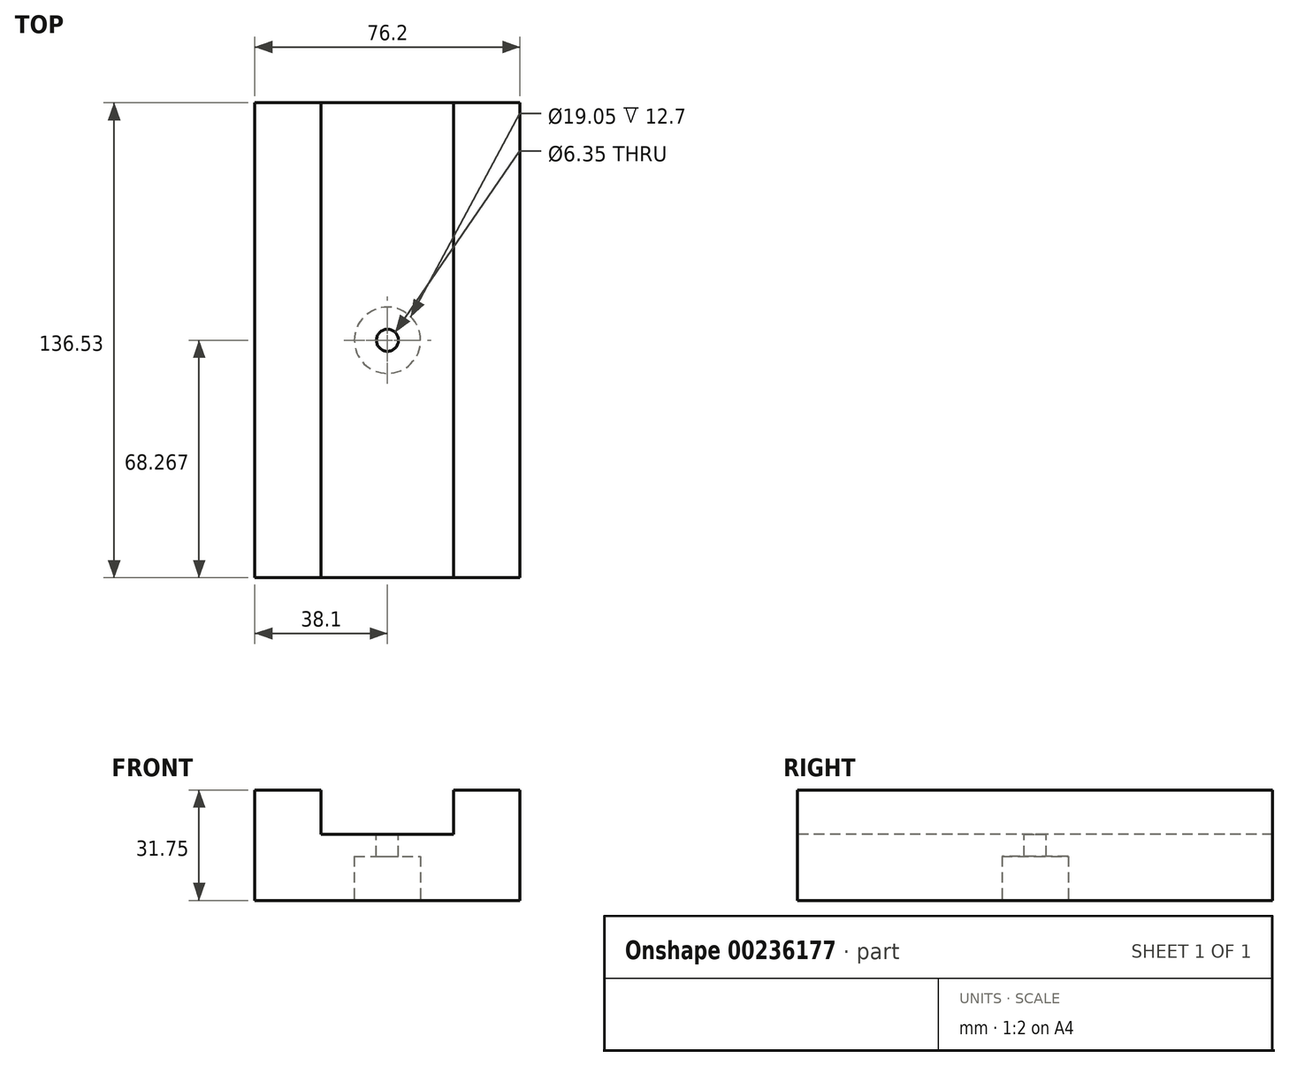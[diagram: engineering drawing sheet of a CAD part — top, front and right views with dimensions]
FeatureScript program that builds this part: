
annotation { "Feature Type Name" : "Feature", "Feature Type Description" : "" }
export const myFeature = defineFeature(function(context is Context, id is Id, definition is map)
    precondition{}
    {
        {
            var Q0;
            Q0=qCreatedBy(makeId("Front.planeOp"),FACE);
            var sketch = newSketch(context, id + "F0", { "sketchPlane" : qUnion([Q0])});
            skLineSegment(sketch, "E0", {"start": v(0, 0) * mm, "end": v(0, -31.75) * mm});
            skLineSegment(sketch, "E1", {"start": v(0, -31.75) * mm, "end": v(76.2, -31.75) * mm});
            skLineSegment(sketch, "E2", {"start": v(76.2, -31.75) * mm, "end": v(76.2, 0) * mm});
            skLineSegment(sketch, "E3", {"start": v(76.2, 0) * mm, "end": v(0, 0) * mm});
            skSolve(sketch);
        }
        {
            var Q0;
            Q0 = qSketchRegion(id + "F0", true);
            extrude(context, id + "F1", {"entities" : qUnion([Q0]), "depth" : 136.53 * mm});
        }
        {
            var Q0;
            Q0=makeQuery(id+"F1.opExtrude","CAP_FACE",FACE,{"disambiguationData":[OSD([sQuery(id+"F0.wireOp",EDGE,"E0"),sQuery(id+"F0.wireOp",EDGE,"E1"),sQuery(id+"F0.wireOp",EDGE,"E2"),sQuery(id+"F0.wireOp",EDGE,"E3")])],"isStart":false});
            var sketch = newSketch(context, id + "F2", { "sketchPlane" : qUnion([Q0])});
            skLineSegment(sketch, "E4", {"start": v(0, 0) * mm, "end": v(19.05, 0) * mm});
            skLineSegment(sketch, "E5", {"start": v(19.05, 0) * mm, "end": v(19.05, -12.7) * mm});
            skLineSegment(sketch, "E6", {"start": v(19.05, -12.7) * mm, "end": v(57.15, -12.7) * mm});
            skLineSegment(sketch, "E7", {"start": v(57.15, -12.7) * mm, "end": v(57.15, 0) * mm});
            skSolve(sketch);
        }
        {
            var Q0;
            {var subQ0=sQuery(id+"F2.wireOp",EDGE,"E5");Q0=makeQuery(id+"F2.imprint","IMPRINT",FACE,{"disambiguationData":[TD([[makeQuery(id+"F2.imprint","IMPRINT",EDGE,{"derivedFrom":subQ0}),1.0]])]});}
            extrude(context, id + "F3", {"entities" : qUnion([Q0]), "operationType" : NewBodyOperationType.REMOVE, "oppositeDirection" : true, "depth" : 254 * mm});
        }
        {
            var Q0;
            Q0=makeQuery(id+"F1.opExtrude","SWEPT_FACE",FACE,{"disambiguationData":[OSD([sQuery(id+"F0.wireOp",EDGE,"E1")])]});
            var sketch = newSketch(context, id + "F4", { "sketchPlane" : qUnion([Q0])});
            skCircle(sketch, "E8", {"center": v(38.1, 68.26) * mm, "radius": 9.53 * mm});
            skPoint(sketch, "E8.centerSnap0", {"position": v(0, 68.26) * mm});
            skPoint(sketch, "E8.centerSnap1", {"position": v(38.1, 136.53) * mm});
            skSolve(sketch);
        }
        {
            var Q0;
            Q0=makeQuery(id+"F4.imprint","IMPRINT",FACE,{"disambiguationData":[TD([[makeQuery(id+"F4.imprint","IMPRINT",EDGE,{"derivedFrom":sQuery(id+"F4.wireOp",EDGE,"E8")}),1.0]])]});
            extrude(context, id + "F5", {"entities" : qUnion([Q0]), "operationType" : NewBodyOperationType.REMOVE, "oppositeDirection" : true, "depth" : 12.7 * mm});
        }
        {
            var Q0;
            Q0=makeQuery(id+"F3.boolean.opBoolean","COPY",FACE,{"derivedFrom":makeQuery(id+"F3.opExtrude","SWEPT_FACE",FACE,{"disambiguationData":[OSD([sQuery(id+"F2.wireOp",EDGE,"E6")])]})});
            var sketch = newSketch(context, id + "F6", { "sketchPlane" : qUnion([Q0])});
            skCircle(sketch, "E9", {"center": v(38.1, -68.26) * mm, "radius": 3.18 * mm});
            skPoint(sketch, "E9.centerSnap0", {"position": v(57.15, -68.26) * mm});
            skPoint(sketch, "E9.centerSnap1", {"position": v(38.1, -136.53) * mm});
            skSolve(sketch);
        }
        {
            var Q0;
            Q0=makeQuery(id+"F6.imprint","IMPRINT",FACE,{"disambiguationData":[TD([[makeQuery(id+"F6.imprint","IMPRINT",EDGE,{"derivedFrom":sQuery(id+"F6.wireOp",EDGE,"E9")}),1.0]])]});
            extrude(context, id + "F7", {"entities" : qUnion([Q0]), "operationType" : NewBodyOperationType.REMOVE, "oppositeDirection" : true, "depth" : 254 * mm});
        }
    });
